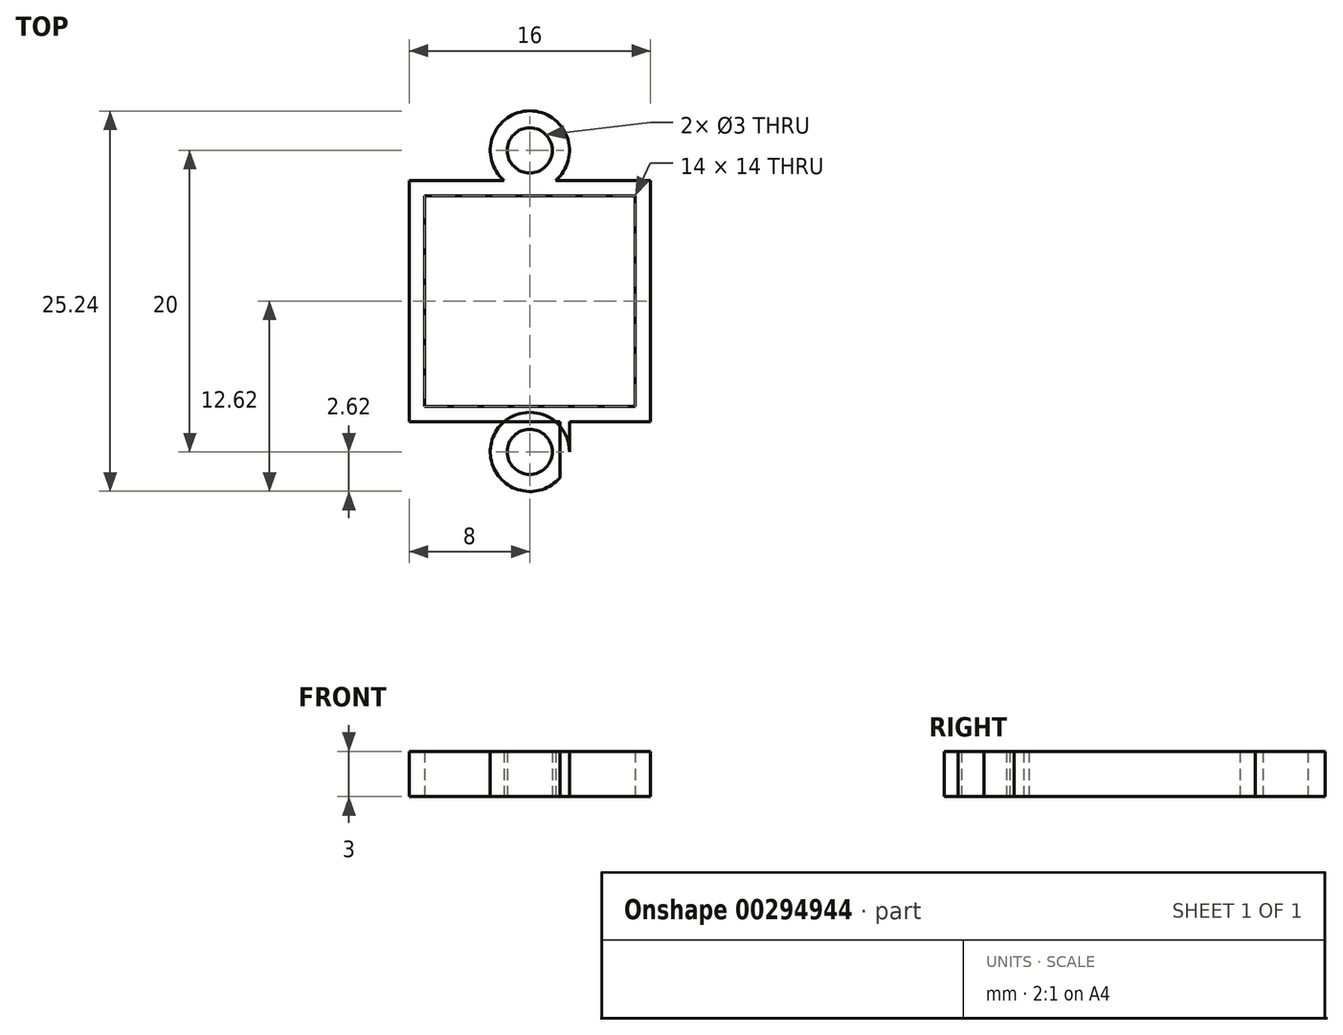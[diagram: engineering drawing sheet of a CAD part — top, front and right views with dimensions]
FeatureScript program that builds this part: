
annotation { "Feature Type Name" : "Feature", "Feature Type Description" : "" }
export const myFeature = defineFeature(function(context is Context, id is Id, definition is map)
    precondition{}
    {
        {
            var Q0;
            Q0=qCreatedBy(makeId("Top.planeOp"),FACE);
            var sketch = newSketch(context, id + "F0", { "sketchPlane" : qUnion([Q0])});
            skLineSegment(sketch, "E0.bottom", {"start": v(8, -8) * mm, "end": v(-8, -8) * mm});
            skLineSegment(sketch, "E0.top", {"start": v(8, 8) * mm, "end": v(-8, 8) * mm});
            skLineSegment(sketch, "E0.left", {"start": v(8, -8) * mm, "end": v(8, 8) * mm});
            skLineSegment(sketch, "E0.right", {"start": v(-8, -8) * mm, "end": v(-8, 8) * mm});
            skPoint(sketch, "E0.middle", {"position": v(0, 0) * mm});
            skLineSegment(sketch, "E1", {"start": v(0, 8) * mm, "end": v(2, 8) * mm});
            skLineSegment(sketch, "E2", {"start": v(0, 8) * mm, "end": v(-2, 8) * mm});
            skLineSegment(sketch, "E3", {"start": v(0, 8) * mm, "end": v(0, 10) * mm});
            skCircle(sketch, "E4", {"center": v(0, 10) * mm, "radius": 1.5 * mm});
            skCircle(sketch, "E5", {"center": v(0, 10) * mm, "radius": 2.62 * mm});
            skLineSegment(sketch, "E6", {"start": v(0, -8) * mm, "end": v(2, -8) * mm});
            skLineSegment(sketch, "E7", {"start": v(0, -8) * mm, "end": v(-2, -8) * mm});
            skLineSegment(sketch, "E8", {"start": v(0, -8) * mm, "end": v(0, -10) * mm});
            skCircle(sketch, "E9", {"center": v(0, -10) * mm, "radius": 1.5 * mm});
            skCircle(sketch, "E10", {"center": v(0, -10) * mm, "radius": 2.62 * mm});
            skLineSegment(sketch, "E11", {"start": v(2, -8) * mm, "end": v(2, -11.7) * mm});
            skLineSegment(sketch, "E12.bottom", {"start": v(7, -7) * mm, "end": v(-7, -7) * mm});
            skLineSegment(sketch, "E12.top", {"start": v(7, 7) * mm, "end": v(-7, 7) * mm});
            skLineSegment(sketch, "E12.left", {"start": v(7, -7) * mm, "end": v(7, 7) * mm});
            skLineSegment(sketch, "E12.right", {"start": v(-7, -7) * mm, "end": v(-7, 7) * mm});
            skLineSegment(sketch, "E13", {"start": v(-2.62, -10) * mm, "end": v(-2.62, -8) * mm});
            skLineSegment(sketch, "E14", {"start": v(2.63, -10) * mm, "end": v(2.63, -8) * mm});
            skLineSegment(sketch, "E15", {"start": v(-2.63, 10) * mm, "end": v(-2.63, 8) * mm});
            skLineSegment(sketch, "E16", {"start": v(2.62, 10) * mm, "end": v(2.62, 8) * mm});
            skSolve(sketch);
        }
        {
            var Q0;
            Q0=makeQuery(id+"F0.imprint","IMPRINT",FACE,{"disambiguationData":[TD([[makeQuery(id+"F0.imprint","IMPRINT",EDGE,{"derivedFrom":sQuery(id+"F0.wireOp",EDGE,"E4")}),-1.0]])]});
            var Q1;
            {var subQ0=sQuery(id+"F0.wireOp",EDGE,"E2");Q1=makeQuery(id+"F0.imprint","IMPRINT",FACE,{"disambiguationData":[TD([[makeQuery(id+"F0.imprint","IMPRINT",EDGE,{"derivedFrom":subQ0}),-1.0]])]});}
            var Q2;
            {var subQ0=sQuery(id+"F0.wireOp",EDGE,"E1");Q2=makeQuery(id+"F0.imprint","IMPRINT",FACE,{"disambiguationData":[TD([[makeQuery(id+"F0.imprint","IMPRINT",EDGE,{"derivedFrom":subQ0}),1.0]])]});}
            var Q3;
            {var subQ4=sQuery(id+"F0.wireOp",EDGE,"E0.left");Q3=makeQuery(id+"F0.imprint","IMPRINT",FACE,{"disambiguationData":[TD([[makeQuery(id+"F0.imprint","IMPRINT",EDGE,{"derivedFrom":subQ4}),1.0]])]});}
            var Q4;
            {var subQ0=sQuery(id+"F0.wireOp",EDGE,"E7");Q4=makeQuery(id+"F0.imprint","IMPRINT",FACE,{"disambiguationData":[TD([[makeQuery(id+"F0.imprint","IMPRINT",EDGE,{"derivedFrom":subQ0}),1.0]])]});}
            var Q5;
            {var subQ0=sQuery(id+"F0.wireOp",EDGE,"E6");Q5=makeQuery(id+"F0.imprint","IMPRINT",FACE,{"disambiguationData":[TD([[makeQuery(id+"F0.imprint","IMPRINT",EDGE,{"derivedFrom":subQ0}),-1.0]])]});}
            var Q6;
            Q6=makeQuery(id+"F0.imprint","IMPRINT",FACE,{"disambiguationData":[TD([[makeQuery(id+"F0.imprint","IMPRINT",EDGE,{"derivedFrom":sQuery(id+"F0.wireOp",EDGE,"E9")}),-1.0]])]});
            var Q7;
            {var subQ0=sQuery(id+"F0.wireOp",EDGE,"9j1caP8V-z49n-FSa5-WNMN-WAUS813RCXMS");var subQ1=sQuery(id+"F0.wireOp",EDGE,"E5");var subQ2=makeQuery(id+"F0.imprint","INTERSECT",VERTEX,{"disambiguationData":[OD(0.0)],"derivedFrom":[subQ1,subQ0]});Q7=makeQuery(id+"F0.imprint","IMPRINT",FACE,{"disambiguationData":[TD([[makeQuery(id+"F0.imprint","IMPRINT",EDGE,{"disambiguationData":[TD([[subQ2,1.0]])],"derivedFrom":subQ1}),1.0]])]});}
            var Q8;
            {var subQ0=sQuery(id+"F0.wireOp",EDGE,"E2");var subQ1=sQuery(id+"F0.wireOp",EDGE,"E1");var subQ2=makeQuery(id+"F0.imprint","INTERSECT",VERTEX,{"derivedFrom":[subQ1,subQ0]});Q8=makeQuery(id+"F0.imprint","IMPRINT",FACE,{"disambiguationData":[TD([[makeQuery(id+"F0.imprint","IMPRINT",EDGE,{"disambiguationData":[TD([[subQ2,-1.0]])],"derivedFrom":subQ1}),-1.0]])]});}
            var Q9;
            {var subQ0=sQuery(id+"F0.wireOp",EDGE,"E7");var subQ1=sQuery(id+"F0.wireOp",EDGE,"E6");var subQ2=makeQuery(id+"F0.imprint","INTERSECT",VERTEX,{"derivedFrom":[subQ1,subQ0]});Q9=makeQuery(id+"F0.imprint","IMPRINT",FACE,{"disambiguationData":[TD([[makeQuery(id+"F0.imprint","IMPRINT",EDGE,{"disambiguationData":[TD([[subQ2,-1.0]])],"derivedFrom":subQ1}),1.0]])]});}
            var Q10;
            {var subQ0=sQuery(id+"F0.wireOp",EDGE,"xbvRovJD-eQ6S-wCiP-dwk6-7ivoR4rX5JBX");var subQ1=sQuery(id+"F0.wireOp",EDGE,"E10");var subQ2=makeQuery(id+"F0.imprint","INTERSECT",VERTEX,{"disambiguationData":[OD(0.0)],"derivedFrom":[subQ1,subQ0]});Q10=makeQuery(id+"F0.imprint","IMPRINT",FACE,{"disambiguationData":[TD([[makeQuery(id+"F0.imprint","IMPRINT",EDGE,{"disambiguationData":[TD([[subQ2,1.0]])],"derivedFrom":subQ1}),1.0]])]});}
            var Q11;
            {var subQ0=sQuery(id+"F0.wireOp",EDGE,"E11");var subQ1=sQuery(id+"F0.wireOp",EDGE,"E10");var subQ2=makeQuery(id+"F0.imprint","INTERSECT",VERTEX,{"disambiguationData":[OD(0.0)],"derivedFrom":[subQ1,subQ0]});Q11=makeQuery(id+"F0.imprint","IMPRINT",FACE,{"disambiguationData":[TD([[makeQuery(id+"F0.imprint","IMPRINT",EDGE,{"disambiguationData":[TD([[subQ2,-1.0]])],"derivedFrom":subQ1}),1.0]])]});}
            var Q12;
            {var subQ3=sQuery(id+"F0.wireOp",EDGE,"E14");Q12=makeQuery(id+"F0.imprint","IMPRINT",FACE,{"disambiguationData":[TD([[makeQuery(id+"F0.imprint","IMPRINT",EDGE,{"derivedFrom":subQ3}),1.0]])]});}
            extrude(context, id + "F1", {"entities" : qUnion([Q0, Q1, Q2, Q3, Q4, Q5, Q6, Q7, Q8, Q9, Q10, Q11, Q12]), "depth" : 3 * mm});
        }
    });
